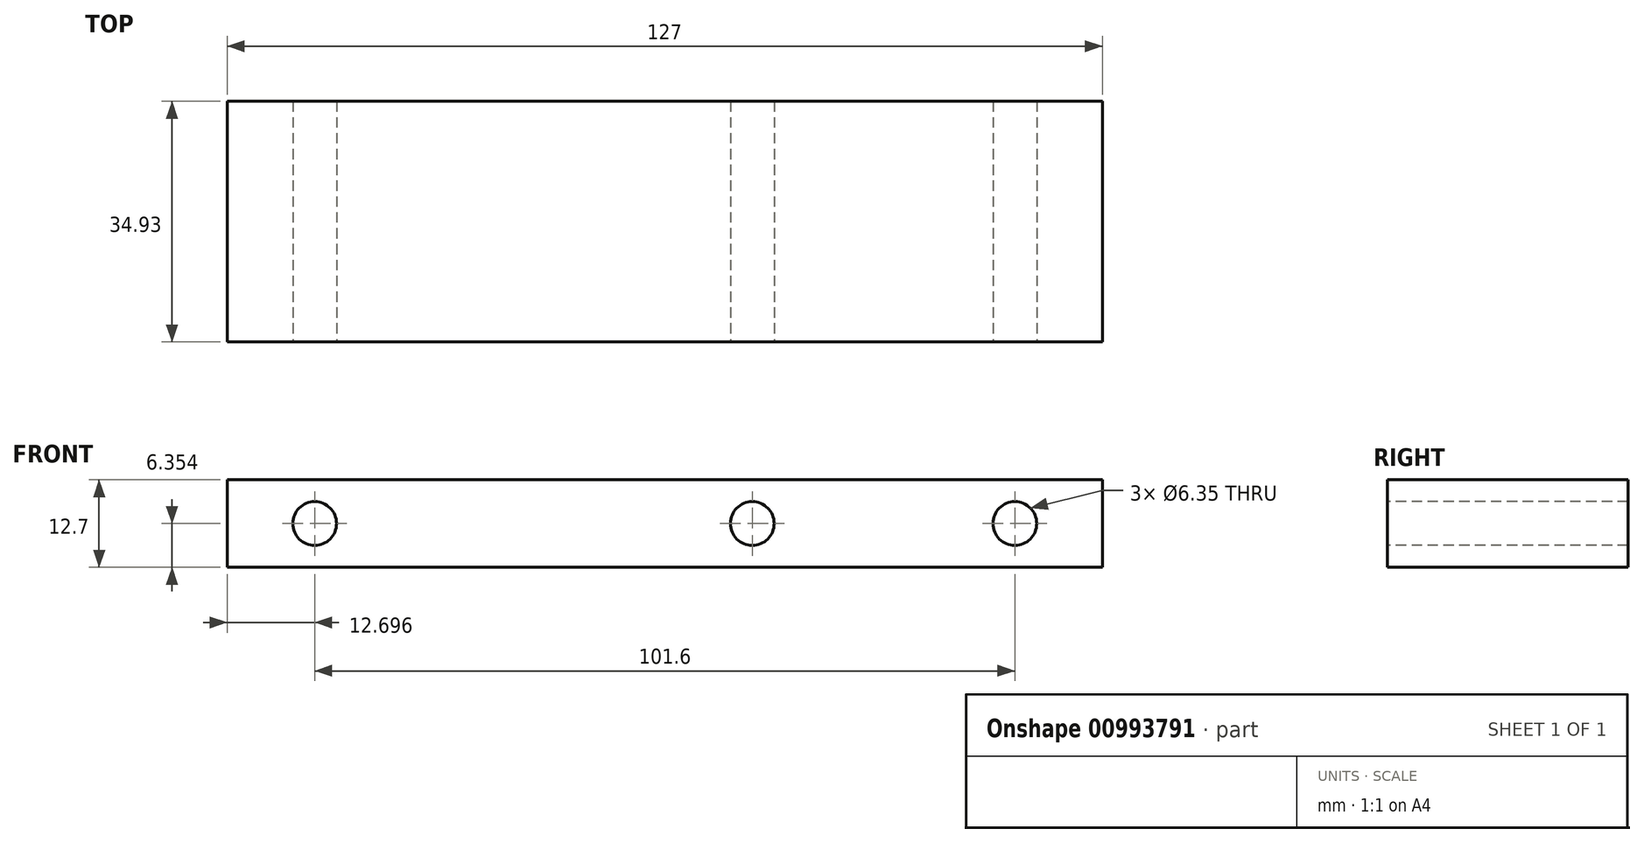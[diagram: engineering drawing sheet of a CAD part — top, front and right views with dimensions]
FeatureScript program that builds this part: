
annotation { "Feature Type Name" : "Feature", "Feature Type Description" : "" }
export const myFeature = defineFeature(function(context is Context, id is Id, definition is map)
    precondition{}
    {
        {
            var Q0;
            Q0=qCreatedBy(makeId("Front.planeOp"),FACE);
            var sketch = newSketch(context, id + "F0", { "sketchPlane" : qUnion([Q0])});
            skLineSegment(sketch, "E0.bottom", {"start": v(-94.55, 42) * mm, "end": v(32.45, 42) * mm});
            skLineSegment(sketch, "E0.top", {"start": v(-94.55, 29.3) * mm, "end": v(32.45, 29.3) * mm});
            skLineSegment(sketch, "E0.left", {"start": v(-94.55, 42) * mm, "end": v(-94.55, 29.3) * mm});
            skLineSegment(sketch, "E0.right", {"start": v(32.45, 42) * mm, "end": v(32.45, 29.3) * mm});
            skSolve(sketch);
        }
        {
            var Q0;
            Q0 = qSketchRegion(id + "F0", true);
            var Q1;
            Q1=makeQuery(id+"F0.imprint","IMPRINT",FACE,{"disambiguationData":[TD([[makeQuery(id+"F0.imprint","IMPRINT",EDGE,{"derivedFrom":sQuery(id+"F0.wireOp",EDGE,"E0.bottom")}),-1.0]])]});
            extrude(context, id + "F1", {"entities" : qUnion([Q0, Q1]), "depth" : 34.92 * mm, "offsetDistance" : 25.4 * mm});
        }
        {
            var Q0;
            Q0=makeQuery(id+"F1.opExtrude","CAP_FACE",FACE,{"disambiguationData":[OSD([sQuery(id+"F0.wireOp",EDGE,"E0.bottom"),sQuery(id+"F0.wireOp",EDGE,"E0.top"),sQuery(id+"F0.wireOp",EDGE,"E0.left"),sQuery(id+"F0.wireOp",EDGE,"E0.right")])],"isStart":false});
            var sketch = newSketch(context, id + "F2", { "sketchPlane" : qUnion([Q0])});
            skCircle(sketch, "E1", {"center": v(-81.85, 35.65) * mm, "radius": 3.18 * mm});
            skCircle(sketch, "E2", {"center": v(-18.35, 35.65) * mm, "radius": 3.18 * mm});
            skCircle(sketch, "E3", {"center": v(19.75, 35.65) * mm, "radius": 3.18 * mm});
            skSolve(sketch);
        }
        {
            var Q0;
            Q0=makeQuery(id+"F2.imprint","IMPRINT",FACE,{"disambiguationData":[TD([[makeQuery(id+"F2.imprint","IMPRINT",EDGE,{"derivedFrom":sQuery(id+"F2.wireOp",EDGE,"E1")}),1.0]])]});
            var Q1;
            Q1=makeQuery(id+"F2.imprint","IMPRINT",FACE,{"disambiguationData":[TD([[makeQuery(id+"F2.imprint","IMPRINT",EDGE,{"derivedFrom":sQuery(id+"F2.wireOp",EDGE,"E2")}),1.0]])]});
            var Q2;
            Q2=makeQuery(id+"F2.imprint","IMPRINT",FACE,{"disambiguationData":[TD([[makeQuery(id+"F2.imprint","IMPRINT",EDGE,{"derivedFrom":sQuery(id+"F2.wireOp",EDGE,"E3")}),1.0]])]});
            var Q3;
            Q3=makeQuery(id+"F2.imprint","IMPRINT",FACE,{"disambiguationData":[TD([[makeQuery(id+"F2.imprint","IMPRINT",EDGE,{"derivedFrom":sQuery(id+"F2.wireOp",EDGE,"689696c7-d9fd-4c27-8cfa-5d22fd01e485")}),1.0]])]});
            var Q4;
            Q4=sQuery(id+"F2.wireOp",EDGE,"E1");
            extrude(context, id + "F3", {"entities" : qUnion([Q0, Q1, Q2, Q3]), "operationType" : NewBodyOperationType.REMOVE, "surfaceEntities" : qUnion([Q4]), "oppositeDirection" : true, "depth" : 34.92 * mm, "offsetDistance" : 25.4 * mm});
        }
    });
